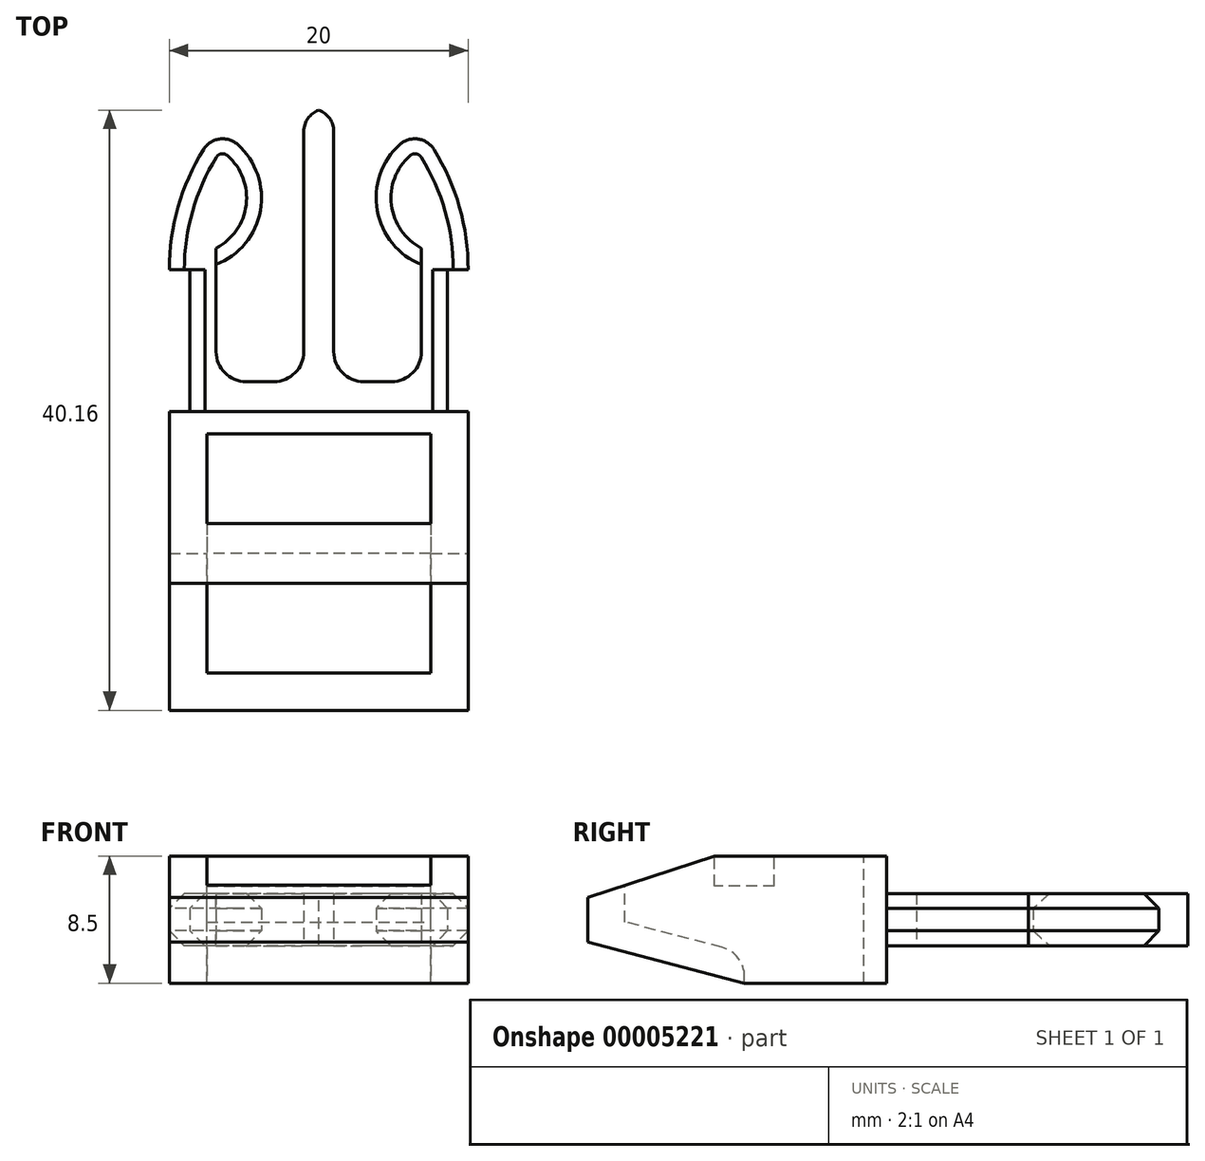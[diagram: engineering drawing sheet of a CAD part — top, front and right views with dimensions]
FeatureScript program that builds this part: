
annotation { "Feature Type Name" : "Feature", "Feature Type Description" : "" }
export const myFeature = defineFeature(function(context is Context, id is Id, definition is map)
    precondition{}
    {
        {
            var Q0;
            Q0=qCreatedBy(makeId("Top.planeOp"),FACE);
            var sketch = newSketch(context, id + "F0", { "sketchPlane" : qUnion([Q0])});
            skLineSegment(sketch, "E0", {"start": v(0, 0) * mm, "end": v(0, 17.8) * mm, "construction": true});
            skLineSegment(sketch, "E1", {"start": v(-10, 0) * mm, "end": v(-10, 20) * mm});
            skLineSegment(sketch, "E2", {"start": v(-10, 20) * mm, "end": v(-8.62, 20) * mm});
            skLineSegment(sketch, "E3", {"start": v(-8.63, 20) * mm, "end": v(-8.63, 29.5) * mm});
            skLineSegment(sketch, "E4", {"start": v(-8.63, 29.5) * mm, "end": v(-10, 29.5) * mm});
            skLineSegment(sketch, "E5", {"start": v(-6.88, 29.83) * mm, "end": v(-6.88, 22) * mm});
            skArc(sketch, "E6", {"start": v(-6.88, 38.75) * mm, "mid": v(-9.2, 34.38) * mm, "end": v(-10, 29.5) * mm});
            skLineSegment(sketch, "E7", {"start": v(-10, 29.5) * mm, "end": v(-10, 23.36) * mm, "construction": true});
            skLineSegment(sketch, "E8", {"start": v(-6.88, 22) * mm, "end": v(-1, 22) * mm});
            skLineSegment(sketch, "E9", {"start": v(-1, 22) * mm, "end": v(-1, 40.25) * mm});
            skLineSegment(sketch, "E10.MirrorCS", {"start": v(10, 0) * mm, "end": v(10, 20) * mm});
            skLineSegment(sketch, "E11.MirrorCS", {"start": v(10, 20) * mm, "end": v(8.62, 20) * mm});
            skLineSegment(sketch, "E12.MirrorCS", {"start": v(8.62, 20) * mm, "end": v(8.62, 29.5) * mm});
            skLineSegment(sketch, "E13.MirrorCS", {"start": v(8.63, 29.5) * mm, "end": v(10, 29.5) * mm});
            skArc(sketch, "E14.MirrorCS", {"start": v(6.87, 38.75) * mm, "mid": v(9.2, 34.38) * mm, "end": v(10, 29.5) * mm});
            skLineSegment(sketch, "E15.MirrorCS", {"start": v(6.88, 29.83) * mm, "end": v(6.88, 22) * mm});
            skLineSegment(sketch, "E16.MirrorCS", {"start": v(6.88, 22) * mm, "end": v(1, 22) * mm});
            skLineSegment(sketch, "E17.MirrorCS", {"start": v(1, 22) * mm, "end": v(1, 40.25) * mm});
            skLineSegment(sketch, "E18", {"start": v(-1, 40.25) * mm, "end": v(1, 40.25) * mm});
            skLineSegment(sketch, "E19", {"start": v(-10, 0) * mm, "end": v(10, 0) * mm});
            skArc(sketch, "E20", {"start": v(-6.88, 29.83) * mm, "mid": v(-3.83, 34.3) * mm, "end": v(-6.88, 38.75) * mm});
            skArc(sketch, "E21.MirrorCS", {"start": v(6.88, 29.83) * mm, "mid": v(3.83, 34.3) * mm, "end": v(6.88, 38.75) * mm});
            skPoint(sketch, "E22.orphan", {"position": v(8.63, 29.5) * mm});
            skSolve(sketch);
        }
        {
            var Q0;
            Q0 = qSketchRegion(id + "F0", true);
            extrude(context, id + "F1", {"entities" : qUnion([Q0]), "depth" : 3.5 * mm, "symmetric" : true});
        }
        {
            var Q0;
            Q0=qCreatedBy(makeId("Top.planeOp"),FACE);
            var sketch = newSketch(context, id + "F2", { "sketchPlane" : qUnion([Q0])});
            skLineSegment(sketch, "E23.0", {"start": v(-10, 0) * mm, "end": v(10, 0) * mm});
            skLineSegment(sketch, "E23.1", {"start": v(-10, 0) * mm, "end": v(-10, 20) * mm});
            skLineSegment(sketch, "E23.2", {"start": v(10, 0) * mm, "end": v(10, 20) * mm});
            skLineSegment(sketch, "E24", {"start": v(-10, 20) * mm, "end": v(10, 20) * mm});
            skSolve(sketch);
        }
        {
            var Q0;
            Q0 = qSketchRegion(id + "F2", true);
            extrude(context, id + "F3", {"entities" : qUnion([Q0]), "operationType" : NewBodyOperationType.ADD, "depth" : 8.5 * mm, "symmetric" : true});
        }
        {
            var Q0;
            Q0=makeQuery(id+"F3.opExtrude","CAP_FACE",FACE,{"disambiguationData":[OSD([sQuery(id+"F2.wireOp",EDGE,"E23.0"),sQuery(id+"F2.wireOp",EDGE,"E23.1"),sQuery(id+"F2.wireOp",EDGE,"E23.2"),sQuery(id+"F2.wireOp",EDGE,"E24")])],"isStart":false});
            var sketch = newSketch(context, id + "F4", { "sketchPlane" : qUnion([Q0])});
            skLineSegment(sketch, "E25.bottom", {"start": v(-7.5, 18.5) * mm, "end": v(7.5, 18.5) * mm});
            skLineSegment(sketch, "E25.top", {"start": v(-7.5, 12.5) * mm, "end": v(7.5, 12.5) * mm});
            skLineSegment(sketch, "E25.left", {"start": v(-7.5, 18.5) * mm, "end": v(-7.5, 12.5) * mm});
            skLineSegment(sketch, "E25.right", {"start": v(7.5, 18.5) * mm, "end": v(7.5, 12.5) * mm});
            skLineSegment(sketch, "E26.bottom", {"start": v(-7.5, 8.5) * mm, "end": v(7.5, 8.5) * mm});
            skLineSegment(sketch, "E26.top", {"start": v(-7.5, 2.5) * mm, "end": v(7.5, 2.5) * mm});
            skLineSegment(sketch, "E26.left", {"start": v(-7.5, 8.5) * mm, "end": v(-7.5, 2.5) * mm});
            skLineSegment(sketch, "E26.right", {"start": v(7.5, 8.5) * mm, "end": v(7.5, 2.5) * mm});
            skSolve(sketch);
        }
        {
            var Q0;
            Q0 = qSketchRegion(id + "F4", true);
            extrude(context, id + "F5", {"entities" : qUnion([Q0]), "operationType" : NewBodyOperationType.REMOVE, "endBound" : BoundingType.THROUGH_ALL, "oppositeDirection" : true, "depth" : 25 * mm});
        }
        {
            var Q0;
            Q0=makeQuery(id+"F5.boolean.opBoolean","COPY",FACE,{"derivedFrom":makeQuery(id+"F5.opExtrude","SWEPT_FACE",FACE,{"disambiguationData":[OSD([sQuery(id+"F4.wireOp",EDGE,"E25.right")])]})});
            var sketch = newSketch(context, id + "F6", { "sketchPlane" : qUnion([Q0])});
            skLineSegment(sketch, "E27.0", {"start": v(-12.5, -4.25) * mm, "end": v(-12.5, 2.25) * mm});
            skLineSegment(sketch, "E27.1", {"start": v(-8.5, -4.25) * mm, "end": v(-8.5, 2.25) * mm});
            skLineSegment(sketch, "E28", {"start": v(-12.5, 2.25) * mm, "end": v(-8.5, 2.25) * mm});
            skLineSegment(sketch, "E29", {"start": v(-12.5, -4.25) * mm, "end": v(-8.5, -4.25) * mm});
            skPoint(sketch, "E30.orphan", {"position": v(-12.5, 4.25) * mm});
            skPoint(sketch, "E31.orphan", {"position": v(-8.5, 4.25) * mm});
            skSolve(sketch);
        }
        {
            var Q0;
            Q0 = qSketchRegion(id + "F6", true);
            var Q1;
            Q1=makeQuery(id+"F5.boolean.opBoolean","COPY",FACE,{"derivedFrom":makeQuery(id+"F5.opExtrude","SWEPT_FACE",FACE,{"disambiguationData":[OSD([sQuery(id+"F4.wireOp",EDGE,"E25.left")])]})});
            extrude(context, id + "F7", {"entities" : qUnion([Q0]), "operationType" : NewBodyOperationType.REMOVE, "endBound" : BoundingType.UP_TO_SURFACE, "endBoundEntityFace" : qUnion([Q1]), "depth" : 25 * mm});
        }
        {
            var Q0;
            Q0=makeQuery(id+"F3.boolean.opBoolean","MERGE",FACE,{"derivedFrom":[makeQuery(id+"F1.opExtrude","SWEPT_FACE",FACE,{"disambiguationData":[OSD([sQuery(id+"F0.wireOp",EDGE,"E1")])]}),makeQuery(id+"F3.opExtrude","SWEPT_FACE",FACE,{"disambiguationData":[OSD([sQuery(id+"F2.wireOp",EDGE,"E23.1")])]})]});
            var sketch = newSketch(context, id + "F8", { "sketchPlane" : qUnion([Q0])});
            skLineSegment(sketch, "E32.0", {"start": v(-12.5, 2.25) * mm, "end": v(-8.5, 2.25) * mm, "construction": true});
            skLineSegment(sketch, "E33.0", {"start": v(-2.5, -4.25) * mm, "end": v(-2.5, 4.25) * mm, "construction": true});
            skLineSegment(sketch, "E34", {"start": v(-2.5, 0) * mm, "end": v(0, 0) * mm, "construction": true});
            skLineSegment(sketch, "E35", {"start": v(0, -1.5) * mm, "end": v(-10.5, -4.25) * mm});
            skLineSegment(sketch, "E36", {"start": v(-10.5, -4.25) * mm, "end": v(-10.5, -2.25) * mm});
            skLineSegment(sketch, "E37", {"start": v(-10.5, -2.25) * mm, "end": v(0, 0.5) * mm});
            skLineSegment(sketch, "E38", {"start": v(0, 0.5) * mm, "end": v(0, -1.5) * mm});
            skPoint(sketch, "E39", {"position": v(-10.5, 2.25) * mm});
            skSolve(sketch);
        }
        {
            var Q0;
            Q0 = qSketchRegion(id + "F8", true);
            var Q1;
            Q1=makeQuery(id+"F3.boolean.opBoolean","MERGE",FACE,{"derivedFrom":[makeQuery(id+"F1.opExtrude","SWEPT_FACE",FACE,{"disambiguationData":[OSD([sQuery(id+"F0.wireOp",EDGE,"E10.MirrorCS")])]}),makeQuery(id+"F3.opExtrude","SWEPT_FACE",FACE,{"disambiguationData":[OSD([sQuery(id+"F2.wireOp",EDGE,"E23.2")])]})]});
            extrude(context, id + "F9", {"entities" : qUnion([Q0]), "operationType" : NewBodyOperationType.ADD, "endBound" : BoundingType.UP_TO_SURFACE, "oppositeDirection" : true, "endBoundEntityFace" : qUnion([Q1]), "depth" : 25 * mm});
        }
        {
            var Q0;
            Q0=makeQuery(id+"F3.boolean.opBoolean","MERGE",FACE,{"derivedFrom":[makeQuery(id+"F1.opExtrude","SWEPT_FACE",FACE,{"disambiguationData":[OSD([sQuery(id+"F0.wireOp",EDGE,"E1")])]}),makeQuery(id+"F3.opExtrude","SWEPT_FACE",FACE,{"disambiguationData":[OSD([sQuery(id+"F2.wireOp",EDGE,"E23.1")])]})]});
            var sketch = newSketch(context, id + "F10", { "sketchPlane" : qUnion([Q0])});
            skLineSegment(sketch, "E40", {"start": v(0, 0) * mm, "end": v(-13.18, 0) * mm, "construction": true});
            skPoint(sketch, "E41.orphan", {"position": v(-10.5, 4.25) * mm});
            skPoint(sketch, "E42.orphan", {"position": v(-10.5, -4.25) * mm});
            skLineSegment(sketch, "E43.0", {"start": v(-8.5, 2.25) * mm, "end": v(-8.5, 4.25) * mm, "construction": true});
            skLineSegment(sketch, "E44", {"start": v(-8.5, 4.25) * mm, "end": v(0, 4.25) * mm});
            skLineSegment(sketch, "E45", {"start": v(0, 4.25) * mm, "end": v(0, 1.5) * mm});
            skLineSegment(sketch, "E46", {"start": v(0, 1.5) * mm, "end": v(-8.5, 4.25) * mm});
            skLineSegment(sketch, "E47.MirrorCS", {"start": v(0, -1.5) * mm, "end": v(-8.5, -4.25) * mm});
            skLineSegment(sketch, "E48.MirrorCS", {"start": v(0, -4.25) * mm, "end": v(0, -1.5) * mm});
            skLineSegment(sketch, "E49.MirrorCS", {"start": v(-8.5, -4.25) * mm, "end": v(0, -4.25) * mm});
            skSolve(sketch);
        }
        {
            var Q0;
            Q0 = qSketchRegion(id + "F10", true);
            extrude(context, id + "F11", {"entities" : qUnion([Q0]), "operationType" : NewBodyOperationType.REMOVE, "endBound" : BoundingType.THROUGH_ALL, "oppositeDirection" : true, "depth" : 25 * mm});
        }
        {
            var Q0;
            Q0=makeQuery(id+"F7.boolean.opBoolean","COPY",EDGE,{"derivedFrom":makeQuery(id+"F7.opExtrude","SWEPT_EDGE",EDGE,{"disambiguationData":[OSD([sQuery(id+"F6.wireOp",EDGE,"E27.1"),sQuery(id+"F6.wireOp",EDGE,"E28")])]})});
            var Q1;
            Q1=makeQuery(id+"F9.opExtrude","SWEPT_EDGE",EDGE,{"disambiguationData":[OSD([sQuery(id+"F8.wireOp",EDGE,"E36"),sQuery(id+"F8.wireOp",EDGE,"E37")])]});
            var Q2;
            Q2=makeQuery(id+"F1.opExtrude","SWEPT_EDGE",EDGE,{"disambiguationData":[OSD([sQuery(id+"F0.wireOp",EDGE,"E16.MirrorCS"),sQuery(id+"F0.wireOp",EDGE,"E17.MirrorCS")])]});
            var Q3;
            Q3=makeQuery(id+"F1.opExtrude","SWEPT_EDGE",EDGE,{"disambiguationData":[OSD([sQuery(id+"F0.wireOp",EDGE,"E8"),sQuery(id+"F0.wireOp",EDGE,"E9")])]});
            var Q4;
            Q4=makeQuery(id+"F1.opExtrude","SWEPT_EDGE",EDGE,{"disambiguationData":[OSD([sQuery(id+"F0.wireOp",EDGE,"E15.MirrorCS"),sQuery(id+"F0.wireOp",EDGE,"E16.MirrorCS")])]});
            var Q5;
            Q5=makeQuery(id+"F1.opExtrude","SWEPT_EDGE",EDGE,{"disambiguationData":[OSD([sQuery(id+"F0.wireOp",EDGE,"E5"),sQuery(id+"F0.wireOp",EDGE,"E8")])]});
            fillet(context, id + "F12", {"entities" : qUnion([Q0, Q1, Q2, Q3, Q4, Q5]), "radius" : 2 * mm, "tangentPropagation" : true, "allowEdgeOverflow" : false});
        }
        {
            var Q0;
            Q0=makeQuery(id+"F1.opExtrude","SWEPT_EDGE",EDGE,{"disambiguationData":[OSD([sQuery(id+"F0.wireOp",EDGE,"E17.MirrorCS"),sQuery(id+"F0.wireOp",EDGE,"E18")])]});
            var Q1;
            Q1=makeQuery(id+"F1.opExtrude","SWEPT_EDGE",EDGE,{"disambiguationData":[OSD([sQuery(id+"F0.wireOp",EDGE,"E9"),sQuery(id+"F0.wireOp",EDGE,"E18")])]});
            var Q2;
            Q2=makeQuery(id+"F1.opExtrude","SWEPT_EDGE",EDGE,{"disambiguationData":[OSD([sQuery(id+"F0.wireOp",EDGE,"E6"),sQuery(id+"F0.wireOp",EDGE,"E20")])]});
            var Q3;
            Q3=makeQuery(id+"F1.opExtrude","SWEPT_EDGE",EDGE,{"disambiguationData":[OSD([sQuery(id+"F0.wireOp",EDGE,"E14.MirrorCS"),sQuery(id+"F0.wireOp",EDGE,"E21.MirrorCS")])]});
            var Q4;
            Q4=makeQuery(id+"F7.boolean.opBoolean","COPY",EDGE,{"derivedFrom":makeQuery(id+"F7.opExtrude","SWEPT_EDGE",EDGE,{"disambiguationData":[OSD([sQuery(id+"F4.wireOp",EDGE,"E25.top"),sQuery(id+"F4.wireOp",EDGE,"E25.right"),sQuery(id+"F6.wireOp",EDGE,"E27.0"),sQuery(id+"F6.wireOp",EDGE,"E28")])]})});
            fillet(context, id + "F13", {"entities" : qUnion([Q0, Q1, Q2, Q3, Q4]), "radius" : 1.5 * mm, "tangentPropagation" : true, "allowEdgeOverflow" : false});
        }
        {
            var Q0;
            {var subQ0=makeQuery(id+"F5.boolean.opBoolean","COPY",FACE,{"derivedFrom":makeQuery(id+"F5.opExtrude","SWEPT_FACE",FACE,{"disambiguationData":[OSD([sQuery(id+"F4.wireOp",EDGE,"E25.left")])]})});var subQ1=makeQuery(id+"F5.boolean.opBoolean","COPY",FACE,{"derivedFrom":makeQuery(id+"F5.opExtrude","SWEPT_FACE",FACE,{"disambiguationData":[OSD([sQuery(id+"F4.wireOp",EDGE,"E26.left")])]})});Q0=makeQuery(id+"F9.boolean.opBoolean","SPLIT",FACE,{"disambiguationData":[TD([makeQuery(id+"F3.opExtrude","CAP_FACE",FACE,{"disambiguationData":[OSD([sQuery(id+"F2.wireOp",EDGE,"E23.0"),sQuery(id+"F2.wireOp",EDGE,"E23.1"),sQuery(id+"F2.wireOp",EDGE,"E23.2"),sQuery(id+"F2.wireOp",EDGE,"E24")])],"isStart":true}),subQ0,makeQuery(id+"F5.boolean.opBoolean","COPY",FACE,{"derivedFrom":makeQuery(id+"F5.opExtrude","SWEPT_FACE",FACE,{"disambiguationData":[OSD([sQuery(id+"F4.wireOp",EDGE,"E26.top")])]})}),subQ1,makeQuery(id+"F9.opExtrude","SWEPT_FACE",FACE,{"disambiguationData":[OSD([sQuery(id+"F8.wireOp",EDGE,"E35")])]}),makeQuery(id+"F9.opExtrude","SWEPT_FACE",FACE,{"disambiguationData":[OSD([sQuery(id+"F8.wireOp",EDGE,"E36")])]})])],"derivedFrom":makeQuery(id+"F7.boolean.opBoolean","MERGE",FACE,{"derivedFrom":[subQ0,subQ1],"fromTools":[makeQuery(id+"F7.opExtrude","CAP_FACE",FACE,{"disambiguationData":[OSD([sQuery(id+"F6.wireOp",EDGE,"E27.0"),sQuery(id+"F6.wireOp",EDGE,"E27.1"),sQuery(id+"F6.wireOp",EDGE,"E28"),sQuery(id+"F6.wireOp",EDGE,"E29")])],"isStart":false})]})});}
            extrude(context, id + "F14", {"entities" : qUnion([Q0]), "operationType" : NewBodyOperationType.REMOVE, "endBound" : BoundingType.THROUGH_ALL, "oppositeDirection" : true, "depth" : 25 * mm, "hasSecondDirection" : true, "secondDirectionBound" : BoundingType.THROUGH_ALL, "secondDirectionOppositeDirection" : false, "secondDirectionDepth" : 25 * mm});
        }
        {
            var Q0;
            Q0=makeQuery(id+"F3.boolean.opBoolean","MERGE",FACE,{"derivedFrom":[makeQuery(id+"F1.opExtrude","SWEPT_FACE",FACE,{"disambiguationData":[OSD([sQuery(id+"F0.wireOp",EDGE,"E1")])]}),makeQuery(id+"F3.opExtrude","SWEPT_FACE",FACE,{"disambiguationData":[OSD([sQuery(id+"F2.wireOp",EDGE,"E23.1")])]})]});
            var sketch = newSketch(context, id + "F15", { "sketchPlane" : qUnion([Q0])});
            skLineSegment(sketch, "E50", {"start": v(-2.5, -2.15) * mm, "end": v(0, -1.5) * mm});
            skLineSegment(sketch, "E51", {"start": v(0, -1.5) * mm, "end": v(-2.5, -2.3) * mm});
            skLineSegment(sketch, "E52", {"start": v(-2.5, -2.3) * mm, "end": v(-2.5, -2.15) * mm});
            skSolve(sketch);
        }
        {
            var Q0;
            Q0 = qSketchRegion(id + "F15", true);
            extrude(context, id + "F16", {"entities" : qUnion([Q0]), "operationType" : NewBodyOperationType.REMOVE, "endBound" : BoundingType.THROUGH_ALL, "oppositeDirection" : true, "depth" : 25 * mm});
        }
        {
            var Q0;
            Q0=makeQuery(id+"F1.opExtrude","CAP_EDGE",EDGE,{"disambiguationData":[OSD([sQuery(id+"F0.wireOp",EDGE,"E14.MirrorCS")])],"isStart":false});
            var Q1;
            Q1=makeQuery(id+"F1.opExtrude","CAP_EDGE",EDGE,{"disambiguationData":[OSD([sQuery(id+"F0.wireOp",EDGE,"E14.MirrorCS")])],"isStart":true});
            var Q2;
            Q2=makeQuery(id+"F1.opExtrude","CAP_EDGE",EDGE,{"disambiguationData":[OSD([sQuery(id+"F0.wireOp",EDGE,"E6")])],"isStart":false});
            var Q3;
            Q3=makeQuery(id+"F1.opExtrude","CAP_EDGE",EDGE,{"disambiguationData":[OSD([sQuery(id+"F0.wireOp",EDGE,"E6")])],"isStart":true});
            var Q4;
            Q4=makeQuery(id+"F1.opExtrude","CAP_EDGE",EDGE,{"disambiguationData":[OSD([sQuery(id+"F0.wireOp",EDGE,"E3")])],"isStart":false});
            var Q5;
            Q5=makeQuery(id+"F1.opExtrude","CAP_EDGE",EDGE,{"disambiguationData":[OSD([sQuery(id+"F0.wireOp",EDGE,"E3")])],"isStart":true});
            var Q6;
            Q6=makeQuery(id+"F1.opExtrude","CAP_EDGE",EDGE,{"disambiguationData":[OSD([sQuery(id+"F0.wireOp",EDGE,"E12.MirrorCS")])],"isStart":false});
            var Q7;
            Q7=makeQuery(id+"F1.opExtrude","CAP_EDGE",EDGE,{"disambiguationData":[OSD([sQuery(id+"F0.wireOp",EDGE,"E12.MirrorCS")])],"isStart":true});
            chamfer(context, id + "F17", {"entities" : qUnion([Q0, Q1, Q2, Q3, Q4, Q5, Q6, Q7]), "width" : 1 * mm, "tangentPropagation" : true});
        }
    });
